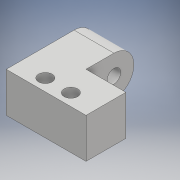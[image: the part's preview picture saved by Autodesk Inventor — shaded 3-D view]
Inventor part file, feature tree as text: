
AUTODESK INVENTOR PART (.ipt)
format: ipt  version: 2017 (Build 210142000, 142)  size: 246,272 bytes
history: native  units: mm
features: extrude x2, sketch x2, fillet x1
ambient origin geometry x8: Origin, YZ Plane, XZ Plane, XY Plane, X Axis, Y Axis, Z Axis, Center Point
bodies: Body1 (feature_tree)
feature tree (5):
  extrude  "押し出し4"  Depth=20.0mm
  extrude  "押し出し5"  Depth=22.0mm
  fillet  "フィレット2"  Radius=12.0mm
  sketch  "スケッチ4"
  sketch  "スケッチ5"
